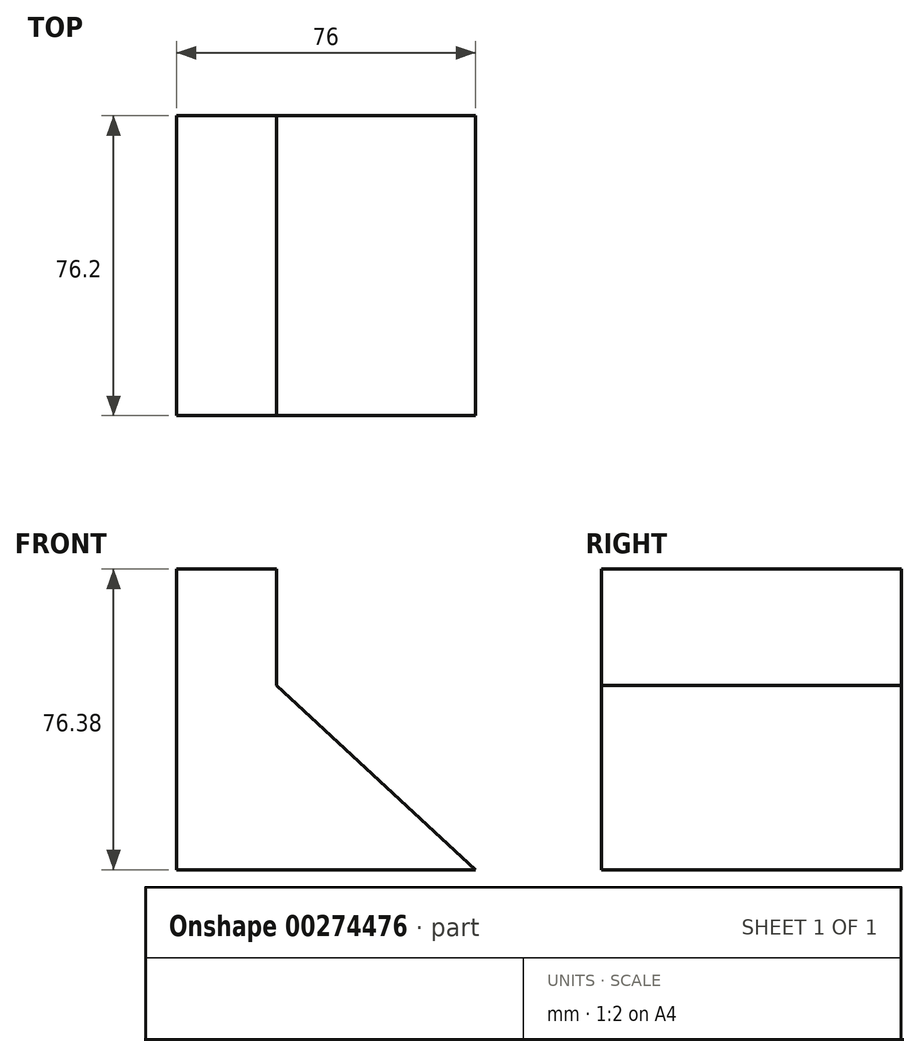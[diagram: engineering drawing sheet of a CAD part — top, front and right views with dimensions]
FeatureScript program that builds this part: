
annotation { "Feature Type Name" : "Feature", "Feature Type Description" : "" }
export const myFeature = defineFeature(function(context is Context, id is Id, definition is map)
    precondition{}
    {
        {
            var Q0;
            Q0=qCreatedBy(makeId("Front.planeOp"),FACE);
            var sketch = newSketch(context, id + "F0", { "sketchPlane" : qUnion([Q0])});
            skLineSegment(sketch, "E0", {"start": v(0, 0) * mm, "end": v(-76, 0) * mm});
            skLineSegment(sketch, "E1", {"start": v(-76, 0) * mm, "end": v(-76, 76.38) * mm});
            skLineSegment(sketch, "E2", {"start": v(-76, 76.38) * mm, "end": v(-50.6, 76.38) * mm});
            skLineSegment(sketch, "E3", {"start": v(-50.6, 76.38) * mm, "end": v(-50.6, 46.78) * mm});
            skLineSegment(sketch, "E4", {"start": v(-50.6, 46.78) * mm, "end": v(0, 0) * mm});
            skSolve(sketch);
        }
        {
            var Q0;
            Q0=makeQuery(id+"F0.imprint","IMPRINT",FACE,{"disambiguationData":[TD([[makeQuery(id+"F0.imprint","IMPRINT",EDGE,{"derivedFrom":sQuery(id+"F0.wireOp",EDGE,"E0")}),-1.0]])]});
            extrude(context, id + "F1", {"entities" : qUnion([Q0]), "depth" : 76.2 * mm});
        }
    });
